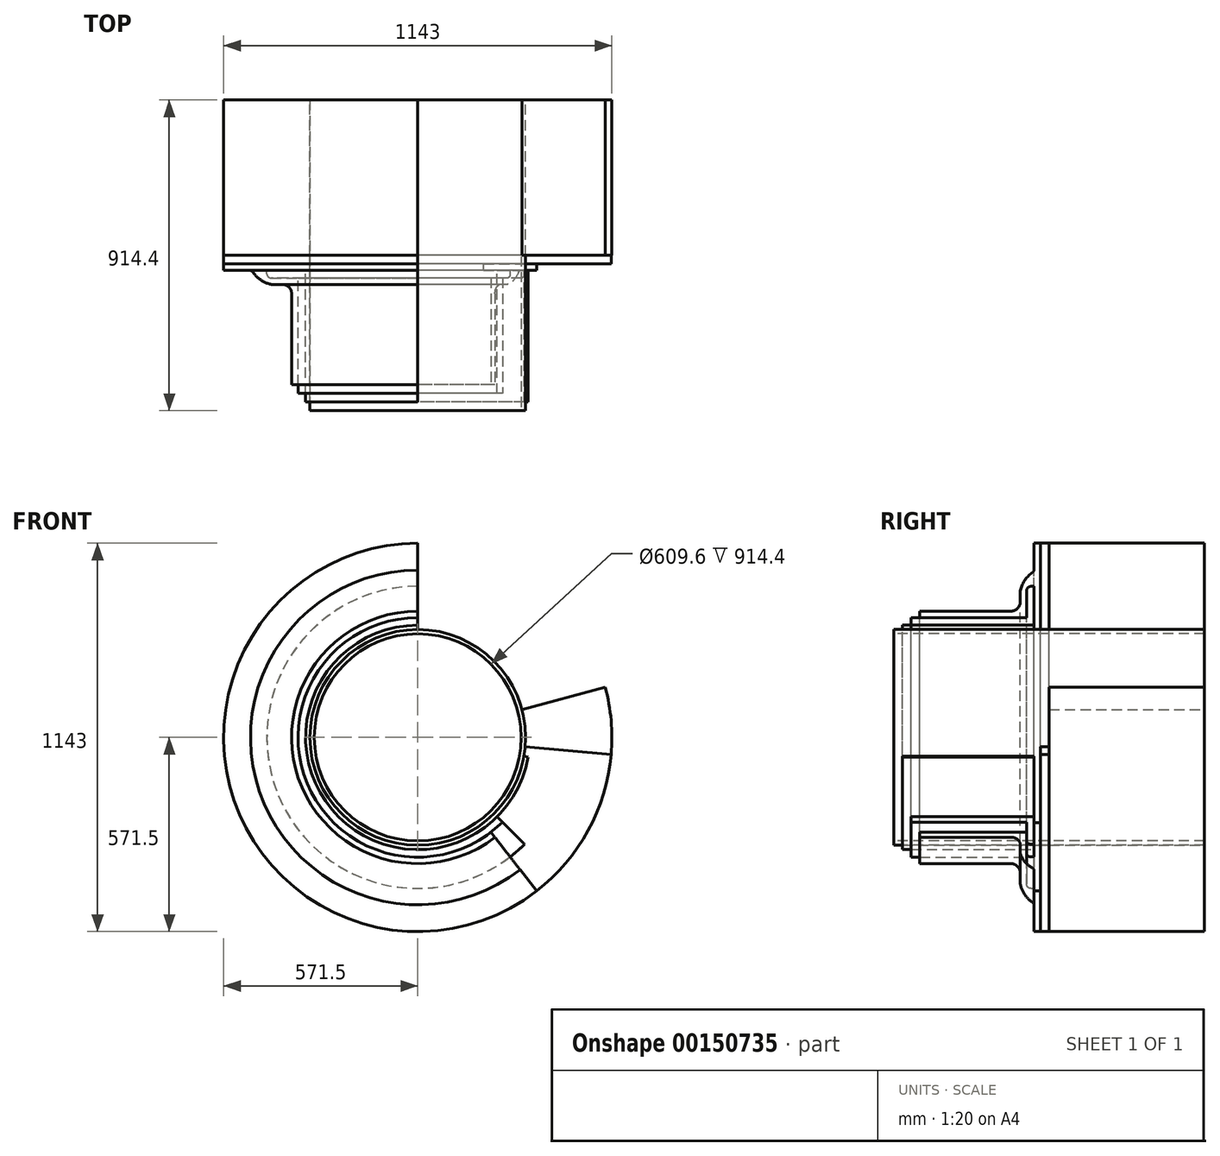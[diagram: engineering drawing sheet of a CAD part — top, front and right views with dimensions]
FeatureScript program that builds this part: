
annotation { "Feature Type Name" : "Feature", "Feature Type Description" : "" }
export const myFeature = defineFeature(function(context is Context, id is Id, definition is map)
    precondition{}
    {
        {
            var Q0;
            Q0=qCreatedBy(makeId("Right.planeOp"),FACE);
            var sketch = newSketch(context, id + "F0", { "sketchPlane" : qUnion([Q0])});
            skLineSegment(sketch, "E0", {"start": v(-457.2, 0) * mm, "end": v(457.2, 0) * mm, "construction": true});
            skLineSegment(sketch, "E1.0", {"start": v(-457.2, 304.8) * mm, "end": v(457.2, 304.8) * mm});
            skLineSegment(sketch, "E2.0", {"start": v(-457.2, 317.5) * mm, "end": v(457.2, 317.5) * mm});
            skLineSegment(sketch, "E3", {"start": v(-457.2, 317.5) * mm, "end": v(-457.2, 304.8) * mm});
            skLineSegment(sketch, "E4", {"start": v(457.2, 317.5) * mm, "end": v(457.2, 304.8) * mm});
            skLineSegment(sketch, "E5", {"start": v(0, 317.5) * mm, "end": v(0, 571.5) * mm});
            skPoint(sketch, "E5.endSnap0", {"position": v(0, 317.5) * mm});
            skLineSegment(sketch, "E6", {"start": v(0, 571.5) * mm, "end": v(457.2, 571.5) * mm});
            skLineSegment(sketch, "E7", {"start": v(457.2, 571.5) * mm, "end": v(457.2, 317.5) * mm});
            skLineSegment(sketch, "E8.0", {"start": v(-25.4, 317.5) * mm, "end": v(-25.4, 571.5) * mm});
            skLineSegment(sketch, "E9", {"start": v(0, 571.5) * mm, "end": v(-25.4, 571.5) * mm});
            skLineSegment(sketch, "E10.0", {"start": v(-44.45, 317.5) * mm, "end": v(-44.45, 444.5) * mm});
            skLineSegment(sketch, "E11", {"start": v(-44.45, 571.5) * mm, "end": v(-25.4, 571.5) * mm});
            skLineSegment(sketch, "E12", {"start": v(-44.45, 444.5) * mm, "end": v(-53.97, 444.5) * mm});
            skPoint(sketch, "E12.endSnap0", {"position": v(-44.45, 444.5) * mm});
            skLineSegment(sketch, "E13", {"start": v(-66.67, 431.8) * mm, "end": v(-66.67, 352.43) * mm});
            skLineSegment(sketch, "E14", {"start": v(-457.2, 330.2) * mm, "end": v(-44.45, 330.2) * mm});
            skLineSegment(sketch, "E15", {"start": v(-66.67, 352.43) * mm, "end": v(-457.2, 352.43) * mm});
            skLineSegment(sketch, "E16", {"start": v(-457.2, 352.43) * mm, "end": v(-457.2, 330.2) * mm});
            skLineSegment(sketch, "E17", {"start": v(-457.2, 330.2) * mm, "end": v(-457.2, 317.5) * mm});
            skLineSegment(sketch, "E18.0", {"start": v(-112.4, 371.48) * mm, "end": v(-457.2, 371.48) * mm});
            skLineSegment(sketch, "E19.0", {"start": v(-85.72, 427.25) * mm, "end": v(-85.72, 398.15) * mm});
            skLineSegment(sketch, "E20", {"start": v(-457.2, 371.48) * mm, "end": v(-457.2, 352.43) * mm});
            skArc(sketch, "E21", {"start": v(-51, 484.2) * mm, "mid": v(-73.32, 460.85) * mm, "end": v(-85.37, 430.9) * mm});
            skPoint(sketch, "E22.visualSharp", {"position": v(-66.67, 444.5) * mm});
            skArc(sketch, "E22.filletArc", {"start": v(-53.97, 444.5) * mm, "mid": v(-62.96, 440.78) * mm, "end": v(-66.67, 431.8) * mm});
            skPoint(sketch, "E23.visualSharp", {"position": v(-61.25, 475.63) * mm});
            skArc(sketch, "E23.filletArc", {"start": v(-51, 484.2) * mm, "mid": v(-47.15, 487.84) * mm, "end": v(-44.45, 492.41) * mm});
            skPoint(sketch, "E24.visualSharp", {"position": v(-85.72, 428.97) * mm});
            skArc(sketch, "E24.filletArc", {"start": v(-85.37, 430.9) * mm, "mid": v(-85.64, 429.08) * mm, "end": v(-85.73, 427.25) * mm});
            skPoint(sketch, "E25.visualSharp", {"position": v(-85.72, 371.48) * mm});
            skArc(sketch, "E25.filletArc", {"start": v(-112.4, 371.48) * mm, "mid": v(-93.54, 379.29) * mm, "end": v(-85.72, 398.15) * mm});
            skLineSegment(sketch, "E26.trimOffspring", {"start": v(-44.45, 492.41) * mm, "end": v(-44.45, 571.5) * mm});
            skSolve(sketch);
        }
        {
            var Q0;
            Q0=makeQuery(id+"F0.imprint","IMPRINT",FACE,{"disambiguationData":[TD([[makeQuery(id+"F0.imprint","IMPRINT",EDGE,{"derivedFrom":sQuery(id+"F0.wireOp",EDGE,"E1.0")}),1.0]])]});
            var Q1;
            Q1=sQuery(id+"F0.wireOp",EDGE,"E0");
            revolve(context, id + "F1", {"entities" : qUnion([Q0]), "axis" : qUnion([Q1]), "revolveType" : RevolveType.FULL});
        }
        {
            var Q0;
            {var subQ2=sQuery(id+"F0.wireOp",EDGE,"E5");Q0=makeQuery(id+"F0.imprint","IMPRINT",FACE,{"disambiguationData":[TD([[makeQuery(id+"F0.imprint","IMPRINT",EDGE,{"derivedFrom":subQ2}),-1.0]])]});}
            var Q1;
            Q1=sQuery(id+"F0.wireOp",EDGE,"E0");
            revolve(context, id + "F2", {"entities" : qUnion([Q0]), "axis" : qUnion([Q1]), "revolveType" : RevolveType.ONE_DIRECTION, "oppositeDirection" : true, "angle" : 285 * degree});
        }
        {
            var Q0;
            {var subQ0=sQuery(id+"F0.wireOp",EDGE,"E5");Q0=makeQuery(id+"F0.imprint","IMPRINT",FACE,{"disambiguationData":[TD([[makeQuery(id+"F0.imprint","IMPRINT",EDGE,{"derivedFrom":subQ0}),1.0]])]});}
            var Q1;
            Q1=sQuery(id+"F0.wireOp",EDGE,"E0");
            revolve(context, id + "F3", {"entities" : qUnion([Q0]), "axis" : qUnion([Q1]), "revolveType" : RevolveType.ONE_DIRECTION, "oppositeDirection" : true, "angle" : 265 * degree});
        }
        {
            var Q0;
            {var subQ1=sQuery(id+"F0.wireOp",EDGE,"E8.0");Q0=makeQuery(id+"F0.imprint","IMPRINT",FACE,{"disambiguationData":[TD([[makeQuery(id+"F0.imprint","IMPRINT",EDGE,{"derivedFrom":subQ1}),1.0]])]});}
            var Q1;
            Q1=makeQuery(id+"F1.opRevolve","SWEPT_FACE",FACE,{"disambiguationData":[OSD([sQuery(id+"F0.wireOp",EDGE,"E1.0")])]});
            revolve(context, id + "F4", {"entities" : qUnion([Q0]), "axis" : qUnion([Q1]), "revolveType" : RevolveType.ONE_DIRECTION, "oppositeDirection" : true, "angle" : 217.72 * degree});
        }
        {
            var Q0;
            {var subQ1=sQuery(id+"F0.wireOp",EDGE,"E12");Q0=makeQuery(id+"F0.imprint","IMPRINT",FACE,{"disambiguationData":[TD([[makeQuery(id+"F0.imprint","IMPRINT",EDGE,{"derivedFrom":subQ1}),1.0]])]});}
            var Q1;
            Q1=sQuery(id+"F0.wireOp",EDGE,"E0");
            revolve(context, id + "F5", {"entities" : qUnion([Q0]), "axis" : qUnion([Q1]), "revolveType" : RevolveType.ONE_DIRECTION, "oppositeDirection" : true, "angle" : 225 * degree});
        }
        {
            var Q0;
            {var subQ4=sQuery(id+"F0.wireOp",EDGE,"E14");Q0=makeQuery(id+"F0.imprint","IMPRINT",FACE,{"disambiguationData":[TD([[makeQuery(id+"F0.imprint","IMPRINT",EDGE,{"derivedFrom":subQ4}),-1.0]])]});}
            var Q1;
            Q1=sQuery(id+"F0.wireOp",EDGE,"E0");
            revolve(context, id + "F6", {"entities" : qUnion([Q0]), "axis" : qUnion([Q1]), "revolveType" : RevolveType.ONE_DIRECTION, "oppositeDirection" : true, "angle" : 260 * degree});
        }
        {
            var Q0;
            Q0=makeQuery(id+"F4.opRevolve","SWEPT_FACE",FACE,{"disambiguationData":[OSD([sQuery(id+"F0.wireOp",EDGE,"E20")])]});
            extrude(context, id + "F7", {"entities" : qUnion([Q0]), "operationType" : NewBodyOperationType.REMOVE, "oppositeDirection" : true, "depth" : 76.2 * mm});
        }
        {
            var Q0;
            Q0=makeQuery(id+"F5.opRevolve","SWEPT_FACE",FACE,{"disambiguationData":[OSD([sQuery(id+"F0.wireOp",EDGE,"E16")])]});
            extrude(context, id + "F8", {"entities" : qUnion([Q0]), "operationType" : NewBodyOperationType.REMOVE, "oppositeDirection" : true, "depth" : 50.8 * mm});
        }
        {
            var Q0;
            Q0=makeQuery(id+"F6.opRevolve","SWEPT_FACE",FACE,{"disambiguationData":[OSD([sQuery(id+"F0.wireOp",EDGE,"E17")])]});
            extrude(context, id + "F9", {"entities" : qUnion([Q0]), "operationType" : NewBodyOperationType.REMOVE, "oppositeDirection" : true, "depth" : 25.4 * mm});
        }
    });
